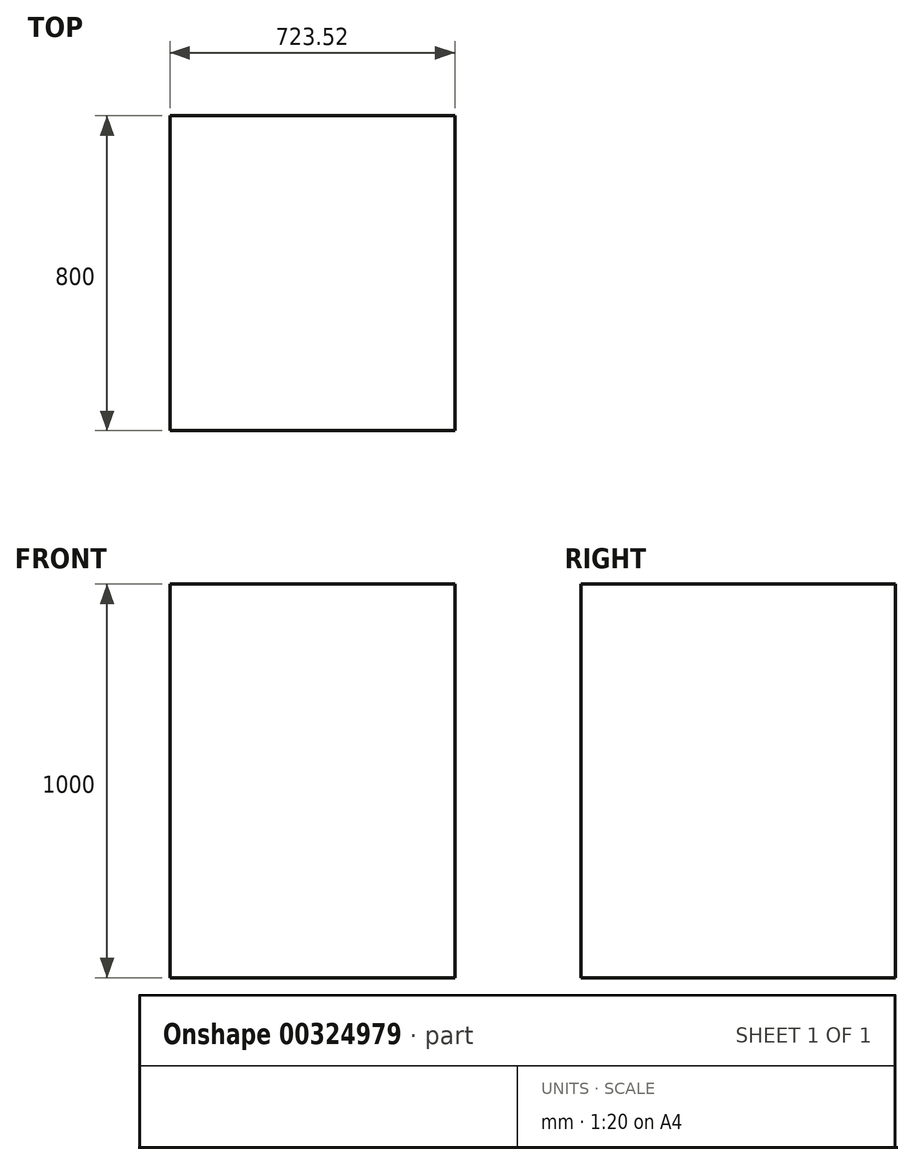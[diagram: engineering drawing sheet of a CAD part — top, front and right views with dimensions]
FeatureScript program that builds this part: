
annotation { "Feature Type Name" : "Feature", "Feature Type Description" : "" }
export const myFeature = defineFeature(function(context is Context, id is Id, definition is map)
    precondition{}
    {
        {
            var Q0;
            Q0=qCreatedBy(makeId("Front.planeOp"),FACE);
            var sketch = newSketch(context, id + "F0", { "sketchPlane" : qUnion([Q0])});
            skLineSegment(sketch, "E0.bottom", {"start": v(-361.76, 500) * mm, "end": v(361.76, 500) * mm});
            skLineSegment(sketch, "E0.top", {"start": v(-361.76, -500) * mm, "end": v(361.76, -500) * mm});
            skLineSegment(sketch, "E0.left", {"start": v(-361.76, 500) * mm, "end": v(-361.76, -500) * mm});
            skLineSegment(sketch, "E0.right", {"start": v(361.76, 500) * mm, "end": v(361.76, -500) * mm});
            skPoint(sketch, "E0.middle", {"position": v(0, 0) * mm});
            skSolve(sketch);
        }
        {
            var Q0;
            Q0=makeQuery(id+"F0.imprint","IMPRINT",FACE,{"disambiguationData":[TD([[makeQuery(id+"F0.imprint","IMPRINT",EDGE,{"derivedFrom":sQuery(id+"F0.wireOp",EDGE,"E0.bottom")}),-1.0]])]});
            extrude(context, id + "F1", {"entities" : qUnion([Q0]), "endBound" : BoundingType.SYMMETRIC, "depth" : 800 * mm, "offsetDistance" : 25 * mm});
        }
    });
